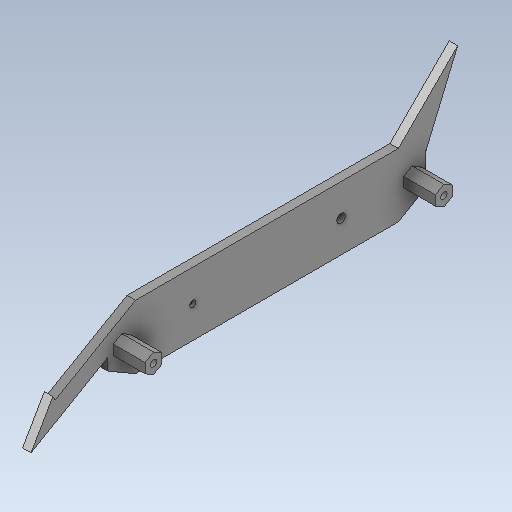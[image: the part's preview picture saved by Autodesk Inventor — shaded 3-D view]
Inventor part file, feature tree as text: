
AUTODESK INVENTOR PART (.ipt)
format: ipt  version: 2020 (Build 240168000, 168)  size: 183,296 bytes
history: native  units: in
note: dims shown in document units (in); Inventor stores cm internally (conversion verified against a paired STEP export)
features: other x3, extrude x2, sketch x2
ambient origin geometry x8: Origin, YZ Plane, XZ Plane, XY Plane, X Axis, Y Axis, Z Axis, Center Point
bodies: Solid1 (feature_tree)
feature tree (7):
  other  "HexWheelGuard.ipt"
  extrude  "Extrusion1"  TaperAngle=0.0deg  [1 undecoded]
  extrude  "Extrusion2"  Depth=0.5906in
  other  "Solid1::HexWheelGuard.ipt"
  other  "TaggingFeature1"
  sketch  "Sketch1"  dims[d0=0.3937in d6=0.0in d7=0.0in]
  sketch  "Sketch2"  dims[d9=0.315in d10=1.4843in d11=60.0deg d12=0.0787in d13=0.3937in d14=0.0in d20=0.3937in d21=0.5906in d22=1.1024in]
note: 1 required parameter value undecoded (feature->parameter linkage not recoverable at this tier; creation-order binding heuristic only, values carry confidence <= 0.55)
